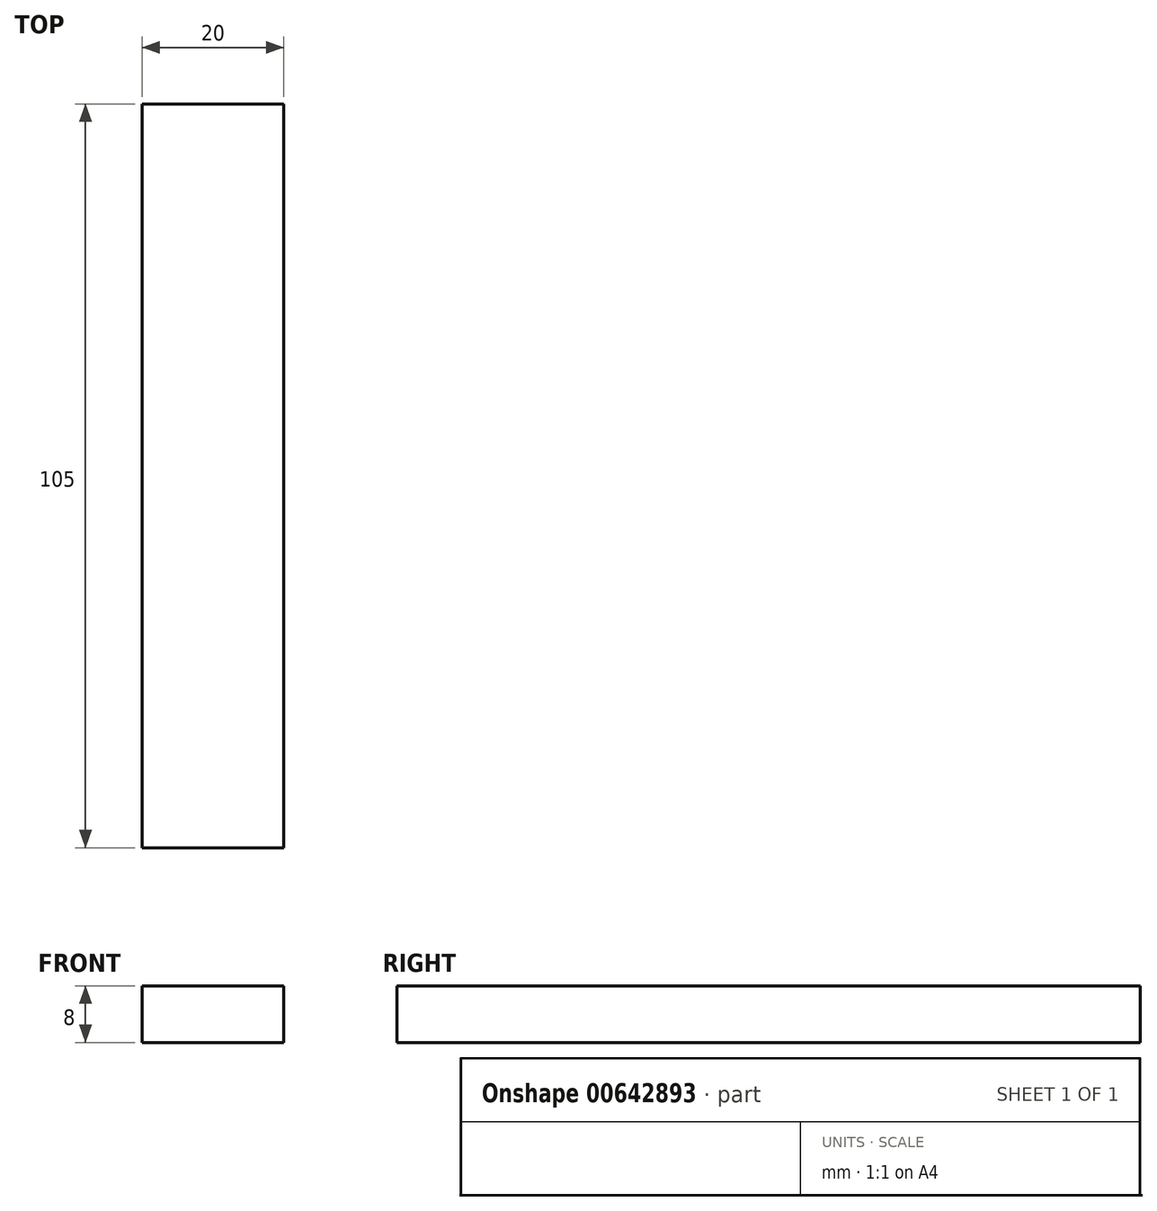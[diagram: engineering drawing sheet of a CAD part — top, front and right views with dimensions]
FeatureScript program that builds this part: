
annotation { "Feature Type Name" : "Feature", "Feature Type Description" : "" }
export const myFeature = defineFeature(function(context is Context, id is Id, definition is map)
    precondition{}
    {
        {
            var Q0;
            Q0=qCreatedBy(makeId("Top.planeOp"),FACE);
            var sketch = newSketch(context, id + "F0", { "sketchPlane" : qUnion([Q0])});
            skLineSegment(sketch, "E0.bottom", {"start": v(0, 0) * mm, "end": v(20, 0) * mm});
            skLineSegment(sketch, "E0.top", {"start": v(0, -105) * mm, "end": v(20, -105) * mm});
            skLineSegment(sketch, "E0.left", {"start": v(0, 0) * mm, "end": v(0, -105) * mm});
            skLineSegment(sketch, "E0.right", {"start": v(20, 0) * mm, "end": v(20, -105) * mm});
            skSolve(sketch);
        }
        {
            var Q0;
            Q0 = qSketchRegion(id + "F0", true);
            extrude(context, id + "F1", {"entities" : qUnion([Q0]), "depth" : 8 * mm, "offsetDistance" : 25.4 * mm});
        }
    });
